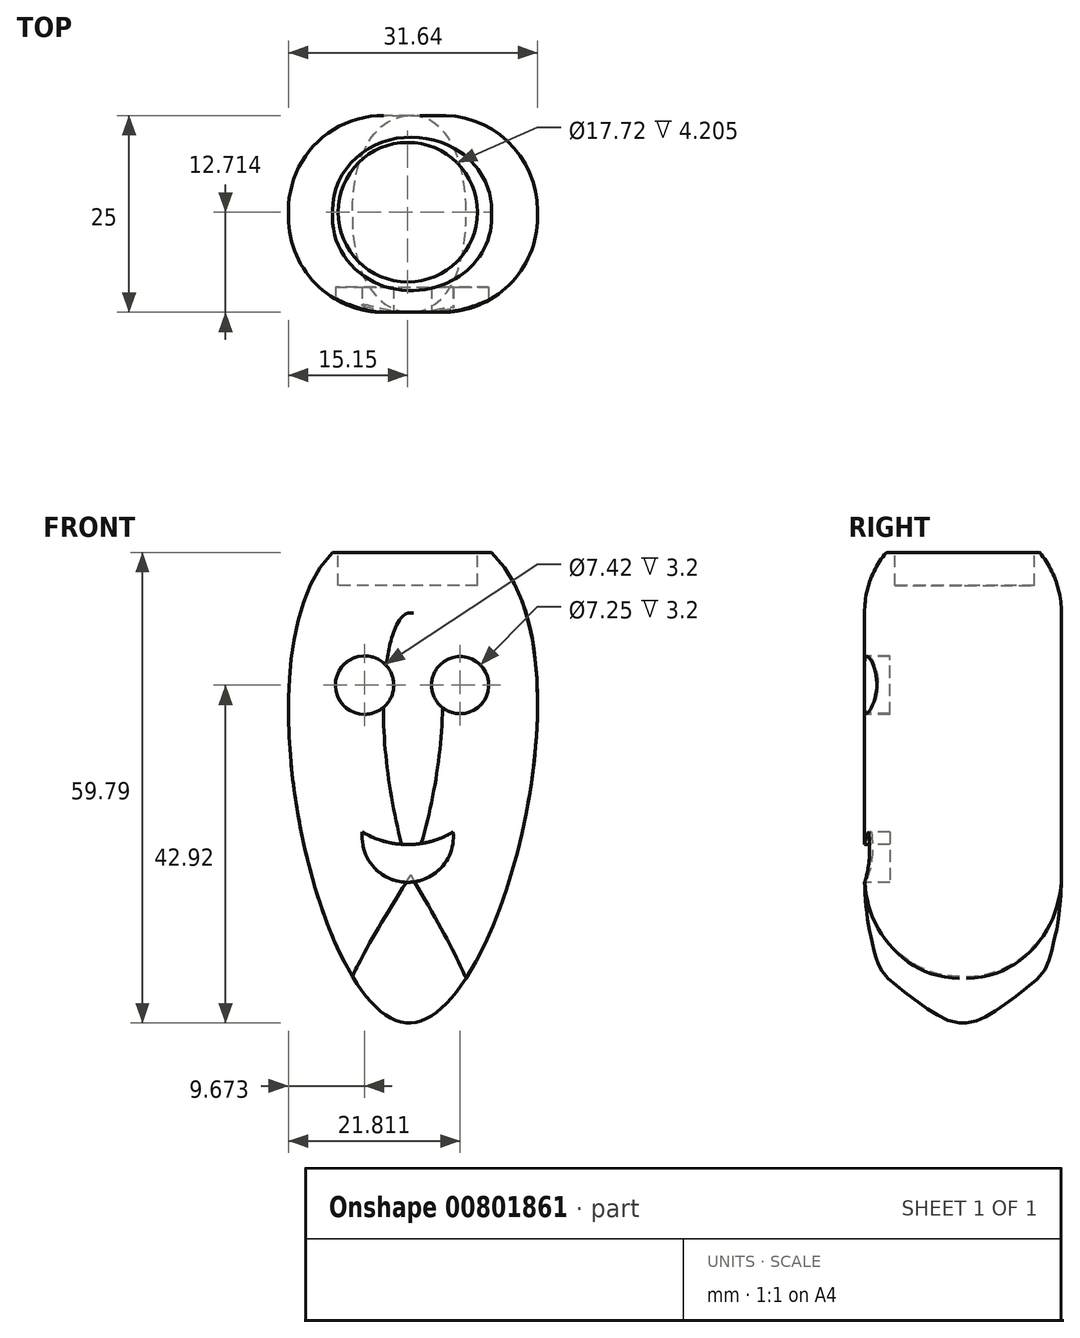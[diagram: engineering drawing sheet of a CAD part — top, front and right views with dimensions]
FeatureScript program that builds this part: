
annotation { "Feature Type Name" : "Feature", "Feature Type Description" : "" }
export const myFeature = defineFeature(function(context is Context, id is Id, definition is map)
    precondition{}
    {
        {
            var Q0;
            Q0=qCreatedBy(makeId("Front.planeOp"),FACE);
            var sketch = newSketch(context, id + "F0", { "sketchPlane" : qUnion([Q0])});
            skFitSpline(sketch, "E0", {"points": [v(-11.74, 22.94) * mm, v(0, -33.88) * mm, v(13.69, 21.63) * mm, v(-11.74, 22.94) * mm]});
            skSolve(sketch);
        }
        {
            var Q0;
            Q0=makeQuery(id+"F0.imprint","IMPRINT",FACE,{"disambiguationData":[TD([[makeQuery(id+"F0.imprint","IMPRINT",EDGE,{"derivedFrom":sQuery(id+"F0.wireOp",EDGE,"E0")}),1.0]])]});
            extrude(context, id + "F1", {"entities" : qUnion([Q0]), "depth" : 25 * mm, "offsetDistance" : 25 * mm});
        }
        {
            var Q0;
            Q0=makeQuery(id+"F1.opExtrude","CAP_EDGE",EDGE,{"disambiguationData":[OSD([sQuery(id+"F0.wireOp",EDGE,"E0")])],"isStart":false});
            var Q1;
            Q1=makeQuery(id+"F1.opExtrude","CAP_EDGE",EDGE,{"disambiguationData":[OSD([sQuery(id+"F0.wireOp",EDGE,"E0")])],"isStart":true});
            fillet(context, id + "F2", {"entities" : qUnion([Q0, Q1]), "radius" : 12.07 * mm, "tangentPropagation" : true, "allowEdgeOverflow" : false});
        }
        {
            var Q0;
            Q0=qCreatedBy(makeId("Top.planeOp"),FACE);
            cPlane(context, id + "F3", {"entities" : qUnion([Q0]), "cplaneType" : CPlaneType.OFFSET, "offset" : 36.6 * mm, "width" : 150 * mm, "height" : 150 * mm});
        }
        {
            var Q0;
            Q0=qCreatedBy(id+"F3.planeOp",FACE);
            var sketch = newSketch(context, id + "F4", { "sketchPlane" : qUnion([Q0])});
            skCircle(sketch, "E1", {"center": v(0, -12.29) * mm, "radius": 8.86 * mm});
            skSolve(sketch);
        }
        {
            var Q0;
            Q0 = qSketchRegion(id + "F4", true);
            extrude(context, id + "F5", {"entities" : qUnion([Q0]), "operationType" : NewBodyOperationType.REMOVE, "oppositeDirection" : true, "depth" : 14.9 * mm, "offsetDistance" : 25 * mm});
        }
        {
            var Q0;
            Q0=qCreatedBy(makeId("Front.planeOp"),FACE);
            var sketch = newSketch(context, id + "F6", { "sketchPlane" : qUnion([Q0])});
            skLineSegment(sketch, "E2.bottom", {"start": v(-22.35, 46.92) * mm, "end": v(21.17, 46.92) * mm});
            skLineSegment(sketch, "E2.top", {"start": v(-22.35, 25.9) * mm, "end": v(21.17, 25.9) * mm});
            skLineSegment(sketch, "E2.left", {"start": v(-22.35, 46.92) * mm, "end": v(-22.35, 25.9) * mm});
            skLineSegment(sketch, "E2.right", {"start": v(21.17, 46.92) * mm, "end": v(21.17, 25.9) * mm});
            skSolve(sketch);
        }
        {
            var Q0;
            Q0 = qSketchRegion(id + "F6", true);
            extrude(context, id + "F7", {"entities" : qUnion([Q0]), "operationType" : NewBodyOperationType.REMOVE, "depth" : 32.6 * mm, "offsetDistance" : 25 * mm});
        }
        {
            var Q0;
            Q0=qCreatedBy(makeId("Front.planeOp"),FACE);
            cPlane(context, id + "F8", {"entities" : qUnion([Q0]), "cplaneType" : CPlaneType.OFFSET, "offset" : 27.4 * mm, "width" : 150 * mm, "height" : 150 * mm});
        }
        {
            var Q0;
            Q0=qCreatedBy(id+"F8.planeOp",FACE);
            var sketch = newSketch(context, id + "F9", { "sketchPlane" : qUnion([Q0])});
            skCircle(sketch, "E3", {"center": v(-5.48, 9.03) * mm, "radius": 3.7 * mm});
            skCircle(sketch, "E4", {"center": v(6.66, 9.03) * mm, "radius": 3.63 * mm});
            skArc(sketch, "E5", {"start": v(-5.77, -9.62) * mm, "mid": v(0, -16.02) * mm, "end": v(5.77, -9.62) * mm});
            skArc(sketch, "E6", {"start": v(-5.77, -9.62) * mm, "mid": v(0, -11.22) * mm, "end": v(5.77, -9.62) * mm});
            skSolve(sketch);
        }
        {
            var Q0;
            Q0=makeQuery(id+"F9.imprint","IMPRINT",FACE,{"disambiguationData":[TD([[makeQuery(id+"F9.imprint","IMPRINT",EDGE,{"derivedFrom":sQuery(id+"F9.wireOp",EDGE,"E3")}),1.0]])]});
            var Q1;
            Q1=makeQuery(id+"F9.imprint","IMPRINT",FACE,{"disambiguationData":[TD([[makeQuery(id+"F9.imprint","IMPRINT",EDGE,{"derivedFrom":sQuery(id+"F9.wireOp",EDGE,"E4")}),1.0]])]});
            var Q2;
            Q2=makeQuery(id+"F9.imprint","IMPRINT",FACE,{"disambiguationData":[TD([[makeQuery(id+"F9.imprint","IMPRINT",EDGE,{"derivedFrom":sQuery(id+"F9.wireOp",EDGE,"E5")}),1.0]])]});
            extrude(context, id + "F10", {"entities" : qUnion([Q0, Q1, Q2]), "operationType" : NewBodyOperationType.REMOVE, "oppositeDirection" : true, "depth" : 5.6 * mm, "offsetDistance" : 25 * mm});
        }
    });
